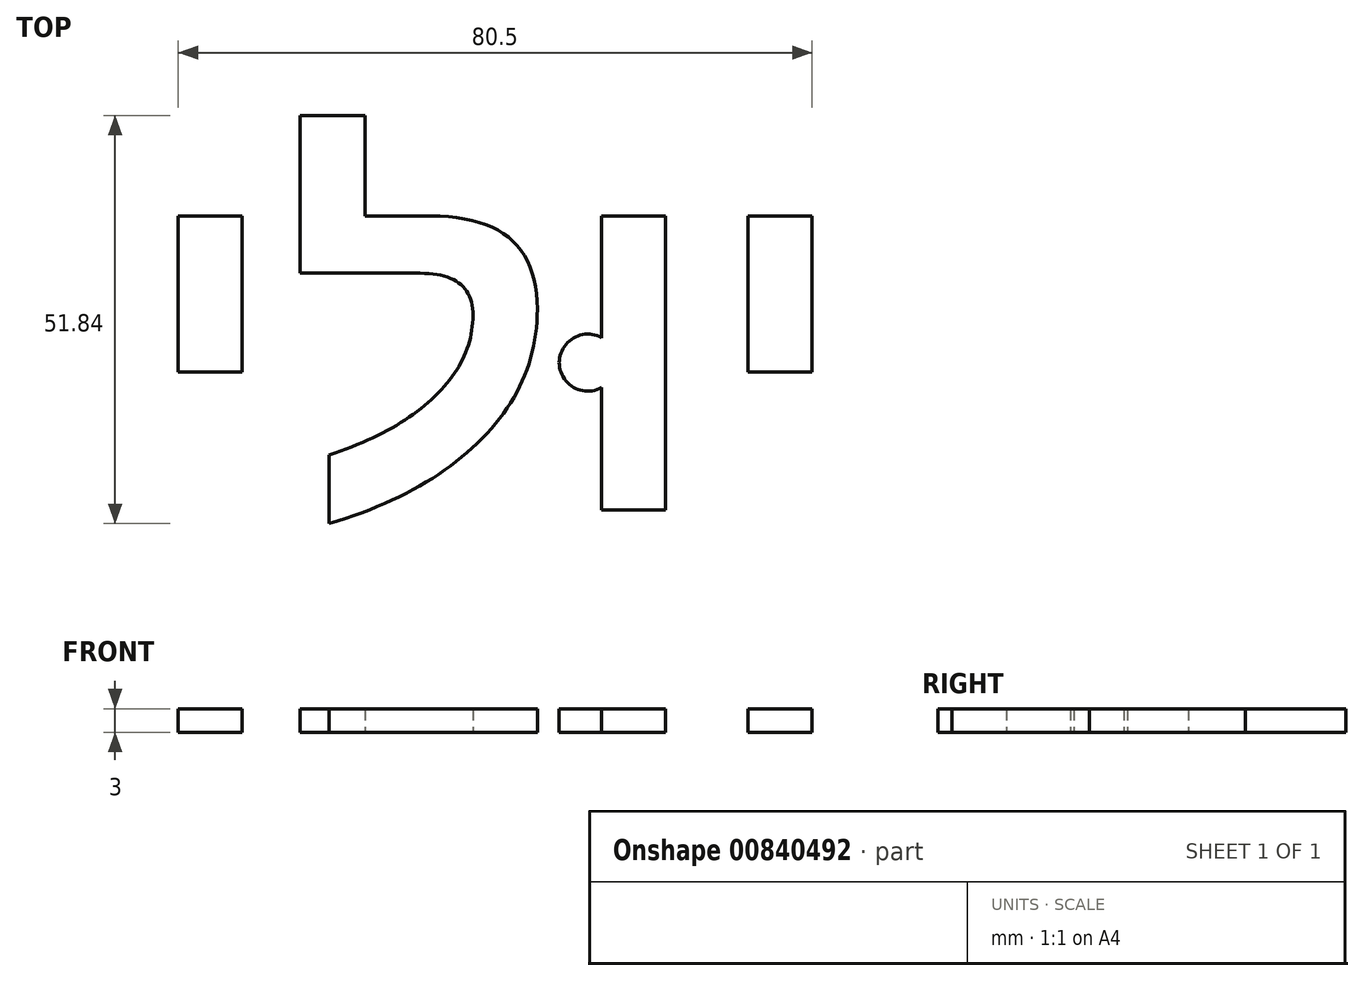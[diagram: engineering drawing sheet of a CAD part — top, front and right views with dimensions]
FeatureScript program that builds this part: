
annotation { "Feature Type Name" : "Feature", "Feature Type Description" : "" }
export const myFeature = defineFeature(function(context is Context, id is Id, definition is map)
    precondition{}
    {
        {
            var Q0;
            Q0=qCreatedBy(makeId("Top.planeOp"),FACE);
            var sketch = newSketch(context, id + "F0", { "sketchPlane" : qUnion([Q0])});
            skText(sketch, "E0", { "text": "ילוי", "fontName": "Arimo-Bold.ttf"});
            const initialGuessF0  = {"E0": [-0.09, 0, 1, 0, 0.04434]};
            skSetInitialGuess(sketch, initialGuessF0);
            skSolve(sketch);
        }
        {
            var Q0;
            Q0 = qSketchRegion(id + "F0", true);
            extrude(context, id + "F1", {"entities" : qUnion([Q0]), "depth" : 3 * mm, "offsetDistance" : 25 * mm});
        }
        {
            var Q0;
            Q0=qCreatedBy(makeId("Top.planeOp"),FACE);
            var sketch = newSketch(context, id + "F2", { "sketchPlane" : qUnion([Q0])});
            skCircle(sketch, "E1", {"center": v(-32.75, 18.69) * mm, "radius": 3.62 * mm});
            skSolve(sketch);
        }
        {
            var Q0;
            Q0 = qSketchRegion(id + "F2", true);
            extrude(context, id + "F3", {"entities" : qUnion([Q0]), "operationType" : NewBodyOperationType.ADD, "depth" : 3 * mm, "offsetDistance" : 25 * mm});
        }
    });
